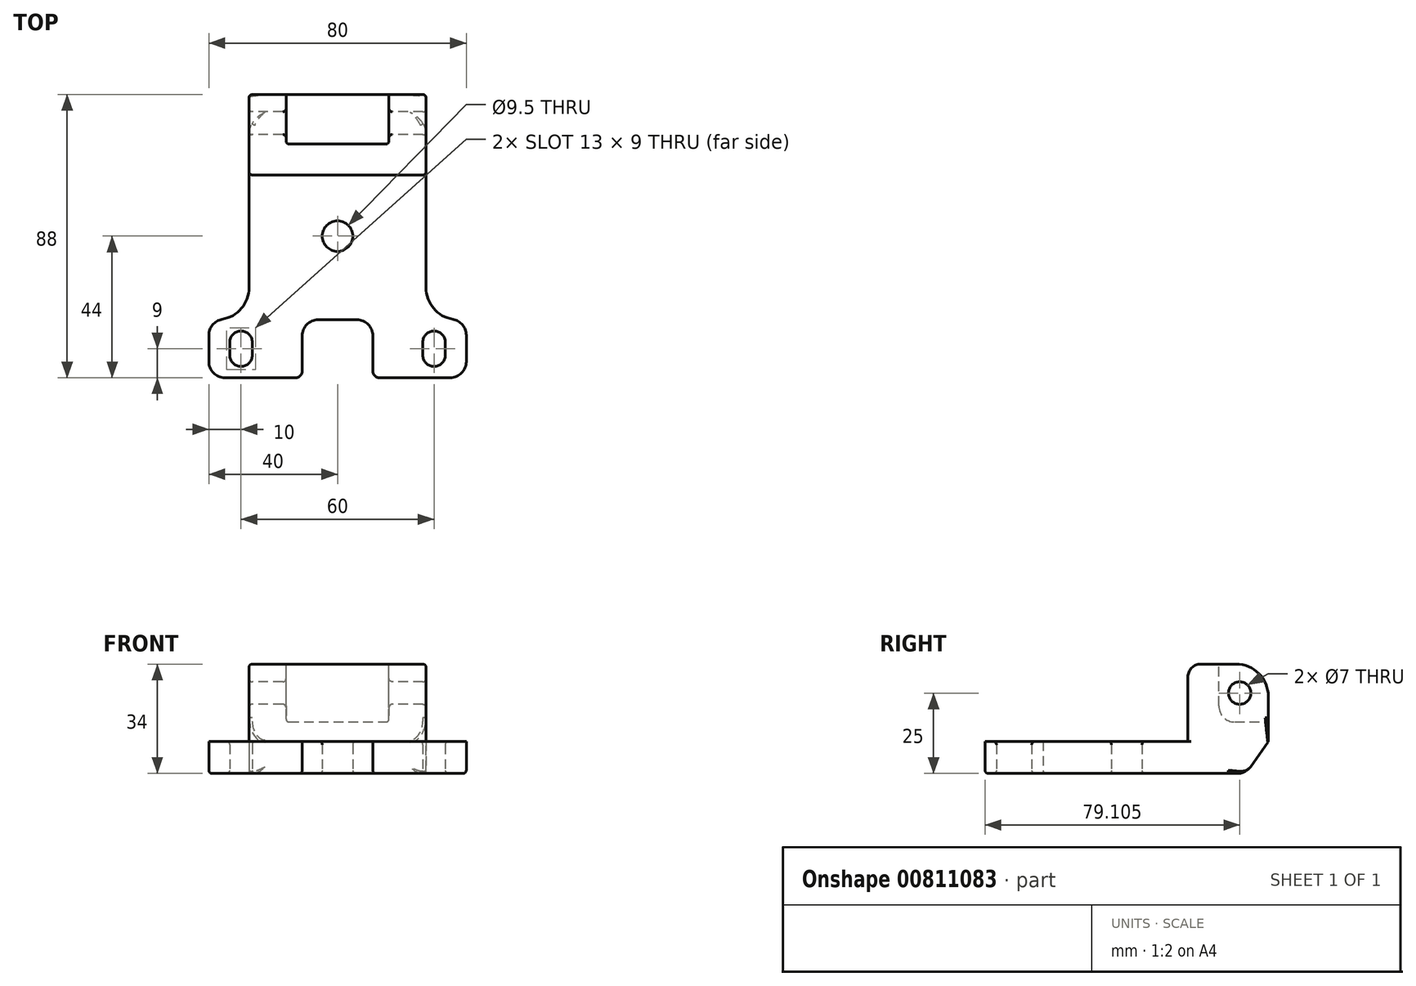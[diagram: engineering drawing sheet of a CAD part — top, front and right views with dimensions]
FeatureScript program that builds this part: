
annotation { "Feature Type Name" : "Feature", "Feature Type Description" : "" }
export const myFeature = defineFeature(function(context is Context, id is Id, definition is map)
    precondition{}
    {
        {
            var Q0;
            Q0=qCreatedBy(makeId("Top.planeOp"),FACE);
            var sketch = newSketch(context, id + "F0", { "sketchPlane" : qUnion([Q0])});
            skLineSegment(sketch, "E0.bottom", {"start": v(-40, 9) * mm, "end": v(-37.5, 9) * mm});
            skLineSegment(sketch, "E0.top", {"start": v(-40, -9) * mm, "end": v(40, -9) * mm});
            skLineSegment(sketch, "E0.left", {"start": v(-40, 9) * mm, "end": v(-40, -9) * mm});
            skLineSegment(sketch, "E0.right", {"start": v(40, 9) * mm, "end": v(40, -9) * mm});
            skPoint(sketch, "E0.middle", {"position": v(0, 0) * mm});
            skLineSegment(sketch, "E1.bottom", {"start": v(37.5, 9) * mm, "end": v(40, 9) * mm});
            skLineSegment(sketch, "E1.top", {"start": v(-27.5, 79) * mm, "end": v(27.5, 79) * mm});
            skLineSegment(sketch, "E1.left", {"start": v(-27.5, 19) * mm, "end": v(-27.5, 79) * mm});
            skLineSegment(sketch, "E1.right", {"start": v(27.5, 19) * mm, "end": v(27.5, 79) * mm});
            skLineSegment(sketch, "E2", {"start": v(0, 0) * mm, "end": v(0, 68.92) * mm, "construction": true});
            skCircle(sketch, "E3", {"center": v(0, 35) * mm, "radius": 4.75 * mm});
            skPoint(sketch, "E4.newPointA", {"position": v(40, 9) * mm});
            skArc(sketch, "E4.filletArc", {"start": v(-37.5, 9) * mm, "mid": v(-30.43, 11.93) * mm, "end": v(-27.5, 19) * mm});
            skPoint(sketch, "E5.visualSharp", {"position": v(27.5, 9) * mm});
            skArc(sketch, "E5.filletArc", {"start": v(27.5, 19) * mm, "mid": v(30.43, 11.93) * mm, "end": v(37.5, 9) * mm});
            skLineSegment(sketch, "E6.bottom", {"start": v(11, 9) * mm, "end": v(-11, 9) * mm});
            skLineSegment(sketch, "E6.top", {"start": v(11, -27) * mm, "end": v(-11, -27) * mm});
            skLineSegment(sketch, "E6.left", {"start": v(11, 9) * mm, "end": v(11, -27) * mm});
            skLineSegment(sketch, "E6.right", {"start": v(-11, 9) * mm, "end": v(-11, -27) * mm});
            skPoint(sketch, "E6.middle", {"position": v(0, -9) * mm});
            skLineSegment(sketch, "E7", {"start": v(-40, 0) * mm, "end": v(40, 0) * mm, "construction": true});
            skCircle(sketch, "E8", {"center": v(-30, 0) * mm, "radius": 3.5 * mm, "construction": true});
            skCircle(sketch, "E9", {"center": v(30, 0) * mm, "radius": 3.5 * mm, "construction": true});
            skLineSegment(sketch, "E10.bottom", {"start": v(-26.5, 2) * mm, "end": v(-33.5, 2) * mm});
            skLineSegment(sketch, "E10.top", {"start": v(-26.5, -2) * mm, "end": v(-33.5, -2) * mm});
            skLineSegment(sketch, "E10.left", {"start": v(-26.5, 2) * mm, "end": v(-26.5, -2) * mm});
            skLineSegment(sketch, "E10.right", {"start": v(-33.5, 2) * mm, "end": v(-33.5, -2) * mm});
            skLineSegment(sketch, "E11.bottom", {"start": v(26.5, 2) * mm, "end": v(33.5, 2) * mm});
            skLineSegment(sketch, "E11.top", {"start": v(26.5, -2) * mm, "end": v(33.5, -2) * mm});
            skLineSegment(sketch, "E11.left", {"start": v(26.5, 2) * mm, "end": v(26.5, -2) * mm});
            skLineSegment(sketch, "E11.right", {"start": v(33.5, 2) * mm, "end": v(33.5, -2) * mm});
            skArc(sketch, "E12", {"start": v(-26.5, 2) * mm, "mid": v(-30, 5.5) * mm, "end": v(-33.5, 2) * mm});
            skArc(sketch, "E13", {"start": v(-33.5, -2) * mm, "mid": v(-30, -5.5) * mm, "end": v(-26.5, -2) * mm});
            skArc(sketch, "E14", {"start": v(33.5, 2) * mm, "mid": v(30, 5.5) * mm, "end": v(26.5, 2) * mm});
            skArc(sketch, "E15", {"start": v(26.5, -2) * mm, "mid": v(30, -5.5) * mm, "end": v(33.5, -2) * mm});
            skSolve(sketch);
        }
        {
            var Q0;
            Q0=makeQuery(id+"F0.imprint","IMPRINT",FACE,{"disambiguationData":[TD([[makeQuery(id+"F0.imprint","IMPRINT",EDGE,{"derivedFrom":sQuery(id+"F0.wireOp",EDGE,"E0.bottom")}),-1.0]])]});
            extrude(context, id + "F1", {"entities" : qUnion([Q0]), "depth" : 10 * mm, "offsetDistance" : 25 * mm});
        }
        {
            var Q0;
            Q0=makeQuery(id+"F1.opExtrude","SWEPT_EDGE",EDGE,{"disambiguationData":[OSD([sQuery(id+"F0.wireOp",EDGE,"E6.bottom"),sQuery(id+"F0.wireOp",EDGE,"E6.left")])]});
            var Q1;
            Q1=makeQuery(id+"F1.opExtrude","SWEPT_EDGE",EDGE,{"disambiguationData":[OSD([sQuery(id+"F0.wireOp",EDGE,"E6.bottom"),sQuery(id+"F0.wireOp",EDGE,"E6.right")])]});
            var Q2;
            Q2=makeQuery(id+"F1.opExtrude","SWEPT_EDGE",EDGE,{"disambiguationData":[OSD([sQuery(id+"F0.wireOp",EDGE,"E0.top"),sQuery(id+"F0.wireOp",EDGE,"E0.right")])]});
            var Q3;
            Q3=makeQuery(id+"F1.opExtrude","SWEPT_EDGE",EDGE,{"disambiguationData":[OSD([sQuery(id+"F0.wireOp",EDGE,"E0.right"),sQuery(id+"F0.wireOp",EDGE,"E1.bottom")])]});
            var Q4;
            Q4=makeQuery(id+"F1.opExtrude","SWEPT_EDGE",EDGE,{"disambiguationData":[OSD([sQuery(id+"F0.wireOp",EDGE,"E0.top"),sQuery(id+"F0.wireOp",EDGE,"E0.left")])]});
            var Q5;
            Q5=makeQuery(id+"F1.opExtrude","SWEPT_EDGE",EDGE,{"disambiguationData":[OSD([sQuery(id+"F0.wireOp",EDGE,"E0.bottom"),sQuery(id+"F0.wireOp",EDGE,"E0.left")])]});
            fillet(context, id + "F2", {"entities" : qUnion([Q0, Q1, Q2, Q3, Q4, Q5]), "radius" : 5 * mm, "tangentPropagation" : true, "allowEdgeOverflow" : false});
        }
        {
            var Q0;
            Q0=makeQuery(id+"F1.opExtrude","SWEPT_EDGE",EDGE,{"disambiguationData":[OSD([sQuery(id+"F0.wireOp",EDGE,"E0.top"),sQuery(id+"F0.wireOp",EDGE,"E6.left")])]});
            var Q1;
            Q1=makeQuery(id+"F1.opExtrude","SWEPT_EDGE",EDGE,{"disambiguationData":[OSD([sQuery(id+"F0.wireOp",EDGE,"E0.top"),sQuery(id+"F0.wireOp",EDGE,"E6.right")])]});
            fillet(context, id + "F3", {"entities" : qUnion([Q0, Q1]), "radius" : 2 * mm, "tangentPropagation" : true, "allowEdgeOverflow" : false});
        }
        {
            var Q0;
            Q0=makeQuery(id+"F1.opExtrude","CAP_FACE",FACE,{"disambiguationData":[OSD([sQuery(id+"F0.wireOp",EDGE,"E0.bottom"),sQuery(id+"F0.wireOp",EDGE,"E0.top"),sQuery(id+"F0.wireOp",EDGE,"E0.left"),sQuery(id+"F0.wireOp",EDGE,"E0.right"),sQuery(id+"F0.wireOp",EDGE,"E1.bottom"),sQuery(id+"F0.wireOp",EDGE,"E1.top"),sQuery(id+"F0.wireOp",EDGE,"E1.left"),sQuery(id+"F0.wireOp",EDGE,"E1.right"),sQuery(id+"F0.wireOp",EDGE,"E3"),sQuery(id+"F0.wireOp",EDGE,"E4.filletArc"),sQuery(id+"F0.wireOp",EDGE,"E5.filletArc"),sQuery(id+"F0.wireOp",EDGE,"E6.bottom"),sQuery(id+"F0.wireOp",EDGE,"E6.left"),sQuery(id+"F0.wireOp",EDGE,"E6.right"),sQuery(id+"F0.wireOp",EDGE,"E8"),sQuery(id+"F0.wireOp",EDGE,"E9")])],"isStart":false});
            var sketch = newSketch(context, id + "F4", { "sketchPlane" : qUnion([Q0])});
            skLineSegment(sketch, "E16.bottom", {"start": v(27.5, 79) * mm, "end": v(-27.5, 79) * mm});
            skLineSegment(sketch, "E16.top", {"start": v(27.5, 54) * mm, "end": v(-27.5, 54) * mm});
            skLineSegment(sketch, "E16.left", {"start": v(27.5, 79) * mm, "end": v(27.5, 54) * mm});
            skLineSegment(sketch, "E16.right", {"start": v(-27.5, 79) * mm, "end": v(-27.5, 54) * mm});
            skSolve(sketch);
        }
        {
            var Q0;
            Q0 = qSketchRegion(id + "F4", true);
            extrude(context, id + "F5", {"entities" : qUnion([Q0]), "operationType" : NewBodyOperationType.ADD, "depth" : 24 * mm, "offsetDistance" : 25 * mm});
        }
        {
            var Q0;
            Q0=makeQuery(id+"F5.boolean.opBoolean","MERGE",FACE,{"derivedFrom":[makeQuery(id+"F1.opExtrude","SWEPT_FACE",FACE,{"disambiguationData":[OSD([sQuery(id+"F0.wireOp",EDGE,"E1.left")])]}),makeQuery(id+"F5.opExtrude","SWEPT_FACE",FACE,{"disambiguationData":[OSD([sQuery(id+"F4.wireOp",EDGE,"E16.right")])]})]});
            var sketch = newSketch(context, id + "F6", { "sketchPlane" : qUnion([Q0])});
            skCircle(sketch, "E17", {"center": v(-70.1, 25) * mm, "radius": 3.5 * mm});
            skLineSegment(sketch, "E18", {"start": v(-66.5, 34) * mm, "end": v(-70.1, 25) * mm, "construction": true});
            skSolve(sketch);
        }
        {
            var Q0;
            Q0 = qSketchRegion(id + "F6", true);
            extrude(context, id + "F7", {"entities" : qUnion([Q0]), "operationType" : NewBodyOperationType.REMOVE, "endBound" : BoundingType.THROUGH_ALL, "oppositeDirection" : true, "depth" : 25 * mm, "offsetDistance" : 25 * mm});
        }
        {
            var Q0;
            {var subQ0=sQuery(id+"F4.wireOp",EDGE,"E16.bottom");var subQ1=sQuery(id+"F4.wireOp",EDGE,"E16.left");var subQ2=sQuery(id+"F4.wireOp",EDGE,"E16.right");Q0=makeQuery(id+"F7.boolean.opBoolean","SPLIT",FACE,{"disambiguationData":[TD([makeQuery(id+"F1.opExtrude","SWEPT_FACE",FACE,{"disambiguationData":[OSD([sQuery(id+"F0.wireOp",EDGE,"E1.top")])]})])],"derivedFrom":makeQuery(id+"F5.opExtrude","CAP_FACE",FACE,{"disambiguationData":[OSD([subQ0,sQuery(id+"F4.wireOp",EDGE,"E16.top"),subQ1,subQ2])],"isStart":false})});}
            var sketch = newSketch(context, id + "F8", { "sketchPlane" : qUnion([Q0])});
            skLineSegment(sketch, "E19.bottom", {"start": v(-16, 63.6) * mm, "end": v(16, 63.6) * mm});
            skLineSegment(sketch, "E19.top", {"start": v(-16, 94.4) * mm, "end": v(16, 94.4) * mm});
            skLineSegment(sketch, "E19.left", {"start": v(-16, 63.6) * mm, "end": v(-16, 94.4) * mm});
            skLineSegment(sketch, "E19.right", {"start": v(16, 63.6) * mm, "end": v(16, 94.4) * mm});
            skPoint(sketch, "E19.middle", {"position": v(0, 79) * mm});
            skSolve(sketch);
        }
        {
            var Q0;
            {var subQ0=sQuery(id+"F8.wireOp",EDGE,"E19.left");var subQ1=sQuery(id+"F4.wireOp",EDGE,"E16.bottom");var subQ4=makeQuery(id+"F5.opExtrude","CAP_EDGE",EDGE,{"disambiguationData":[OSD([subQ1])],"isStart":false});var subQ5=makeQuery(id+"F8.imprint","INTERSECT",VERTEX,{"derivedFrom":[subQ4,subQ0]});Q0=makeQuery(id+"F8.imprint","IMPRINT",FACE,{"disambiguationData":[TD([[makeQuery(id+"F8.imprint","IMPRINT",EDGE,{"disambiguationData":[TD([[subQ5,-1.0]])],"derivedFrom":subQ4}),-1.0]])]});}
            var Q1;
            {var subQ0=sQuery(id+"F8.wireOp",EDGE,"E19.bottom");Q1=makeQuery(id+"F8.imprint","IMPRINT",FACE,{"disambiguationData":[TD([[makeQuery(id+"F8.imprint","IMPRINT",EDGE,{"derivedFrom":subQ0}),1.0]])]});}
            extrude(context, id + "F9", {"entities" : qUnion([Q0, Q1]), "operationType" : NewBodyOperationType.REMOVE, "oppositeDirection" : true, "depth" : 18 * mm, "offsetDistance" : 25 * mm});
        }
        {
            var Q0;
            Q0=makeQuery(id+"F9.boolean.opBoolean","COPY",EDGE,{"derivedFrom":makeQuery(id+"F9.opExtrude","CAP_EDGE",EDGE,{"disambiguationData":[OSD([sQuery(id+"F8.wireOp",EDGE,"E19.bottom")])],"isStart":false})});
            var Q1;
            Q1=makeQuery(id+"F9.boolean.opBoolean","COPY",EDGE,{"derivedFrom":makeQuery(id+"F9.opExtrude","CAP_EDGE",EDGE,{"disambiguationData":[OSD([sQuery(id+"F4.wireOp",EDGE,"E16.bottom")])],"isStart":false})});
            fillet(context, id + "F10", {"entities" : qUnion([Q0, Q1]), "radius" : 5 * mm, "tangentPropagation" : true, "allowEdgeOverflow" : false});
        }
        {
            var Q0;
            Q0=makeQuery(id+"F5.opExtrude","CAP_EDGE",EDGE,{"disambiguationData":[OSD([sQuery(id+"F4.wireOp",EDGE,"E16.top")])],"isStart":true});
            var Q1;
            {var subQ1=sQuery(id+"F4.wireOp",EDGE,"E16.bottom");Q1=makeQuery(id+"F9.boolean.opBoolean","SPLIT",EDGE,{"disambiguationData":[TD([makeQuery(id+"F1.opExtrude","SWEPT_FACE",FACE,{"disambiguationData":[OSD([sQuery(id+"F0.wireOp",EDGE,"E1.left")])]})])],"derivedFrom":makeQuery(id+"F5.opExtrude","CAP_EDGE",EDGE,{"disambiguationData":[OSD([subQ1])],"isStart":false})});}
            var Q2;
            {var subQ1=sQuery(id+"F4.wireOp",EDGE,"E16.bottom");Q2=makeQuery(id+"F9.boolean.opBoolean","SPLIT",EDGE,{"disambiguationData":[TD([makeQuery(id+"F1.opExtrude","SWEPT_FACE",FACE,{"disambiguationData":[OSD([sQuery(id+"F0.wireOp",EDGE,"E1.right")])]})])],"derivedFrom":makeQuery(id+"F5.opExtrude","CAP_EDGE",EDGE,{"disambiguationData":[OSD([subQ1])],"isStart":false})});}
            fillet(context, id + "F11", {"entities" : qUnion([Q0, Q1, Q2]), "radius" : 10 * mm, "tangentPropagation" : true, "allowEdgeOverflow" : false});
        }
        {
            var Q0;
            Q0=makeQuery(id+"F5.opExtrude","CAP_EDGE",EDGE,{"disambiguationData":[OSD([sQuery(id+"F4.wireOp",EDGE,"E16.top")])],"isStart":false});
            var Q1;
            Q1=makeQuery(id+"F9.boolean.opBoolean","COPY",EDGE,{"derivedFrom":makeQuery(id+"F9.opExtrude","CAP_EDGE",EDGE,{"disambiguationData":[OSD([sQuery(id+"F8.wireOp",EDGE,"E19.bottom")])],"isStart":true})});
            fillet(context, id + "F12", {"entities" : qUnion([Q0, Q1]), "radius" : 4 * mm, "tangentPropagation" : true, "allowEdgeOverflow" : false});
        }
        {
            var Q0;
            Q0=makeQuery(id+"F1.opExtrude","CAP_EDGE",EDGE,{"disambiguationData":[OSD([sQuery(id+"F0.wireOp",EDGE,"E1.top")])],"isStart":true});
            chamfer(context, id + "F13", {"entities" : qUnion([Q0]), "chamferType" : ChamferType.TWO_OFFSETS, "width1" : 7 * mm, "oppositeDirection" : false, "width2" : 10 * mm, "tangentPropagation" : true});
        }
        {
            var Q0;
            Q0=makeQuery(id+"F9.boolean.opBoolean","SPLIT",FACE,{"disambiguationData":[TD([makeQuery(id+"F1.opExtrude","SWEPT_FACE",FACE,{"disambiguationData":[OSD([sQuery(id+"F0.wireOp",EDGE,"E1.right")])]})])],"derivedFrom":makeQuery(id+"F7.boolean.opBoolean","COPY",FACE,{"derivedFrom":makeQuery(id+"F7.opExtrude","SWEPT_FACE",FACE,{"disambiguationData":[OSD([sQuery(id+"F6.wireOp",EDGE,"E17")])]})})});
            var Q1;
            Q1=makeQuery(id+"F9.boolean.opBoolean","SPLIT",FACE,{"disambiguationData":[TD([makeQuery(id+"F1.opExtrude","SWEPT_FACE",FACE,{"disambiguationData":[OSD([sQuery(id+"F0.wireOp",EDGE,"E1.left")])]})])],"derivedFrom":makeQuery(id+"F7.boolean.opBoolean","COPY",FACE,{"derivedFrom":makeQuery(id+"F7.opExtrude","SWEPT_FACE",FACE,{"disambiguationData":[OSD([sQuery(id+"F6.wireOp",EDGE,"E17")])]})})});
            var Q2;
            Q2=makeQuery(id+"F1.opExtrude","SWEPT_FACE",FACE,{"disambiguationData":[OSD([sQuery(id+"F0.wireOp",EDGE,"E9")])]});
            var Q3;
            Q3=makeQuery(id+"F1.opExtrude","SWEPT_FACE",FACE,{"disambiguationData":[OSD([sQuery(id+"F0.wireOp",EDGE,"E8")])]});
            var Q4;
            Q4=makeQuery(id+"F1.opExtrude","SWEPT_FACE",FACE,{"disambiguationData":[OSD([sQuery(id+"F0.wireOp",EDGE,"E3")])]});
            var Q5;
            {var subQ0=sQuery(id+"F4.wireOp",EDGE,"E16.right");var subQ1=makeQuery(id+"F5.opExtrude","SWEPT_FACE",FACE,{"disambiguationData":[OSD([subQ0])]});var subQ2=makeQuery(id+"F1.opExtrude","SWEPT_FACE",FACE,{"disambiguationData":[OSD([sQuery(id+"F0.wireOp",EDGE,"E1.left")])]});var subQ3=sQuery(id+"F4.wireOp",EDGE,"E16.bottom");Q5=makeQuery(id+"F11.opFillet","BLEND_EDGE",EDGE,{"blendedFrom":[makeQuery(id+"F9.boolean.opBoolean","SPLIT",EDGE,{"disambiguationData":[TD([subQ2])],"derivedFrom":makeQuery(id+"F5.opExtrude","CAP_EDGE",EDGE,{"disambiguationData":[OSD([subQ3])],"isStart":false})}),makeQuery(id+"F5.boolean.opBoolean","MERGE",FACE,{"derivedFrom":[subQ2,subQ1]})],"blendedInto":[makeQuery(id+"F5.boolean.opBoolean","MERGE",FACE,{"derivedFrom":[subQ2,subQ1]})]});}
            var Q6;
            {var subQ0=sQuery(id+"F4.wireOp",EDGE,"E16.left");var subQ1=makeQuery(id+"F5.opExtrude","SWEPT_FACE",FACE,{"disambiguationData":[OSD([subQ0])]});var subQ2=makeQuery(id+"F1.opExtrude","SWEPT_FACE",FACE,{"disambiguationData":[OSD([sQuery(id+"F0.wireOp",EDGE,"E1.right")])]});var subQ3=sQuery(id+"F4.wireOp",EDGE,"E16.bottom");Q6=makeQuery(id+"F11.opFillet","BLEND_EDGE",EDGE,{"blendedFrom":[makeQuery(id+"F9.boolean.opBoolean","SPLIT",EDGE,{"disambiguationData":[TD([subQ2])],"derivedFrom":makeQuery(id+"F5.opExtrude","CAP_EDGE",EDGE,{"disambiguationData":[OSD([subQ3])],"isStart":false})}),makeQuery(id+"F5.boolean.opBoolean","MERGE",FACE,{"derivedFrom":[subQ2,subQ1]})],"blendedInto":[makeQuery(id+"F5.boolean.opBoolean","MERGE",FACE,{"derivedFrom":[subQ2,subQ1]})]});}
            var Q7;
            Q7=makeQuery(id+"F9.boolean.opBoolean","COPY",EDGE,{"derivedFrom":makeQuery(id+"F9.opExtrude","SWEPT_EDGE",EDGE,{"disambiguationData":[OSD([sQuery(id+"F4.wireOp",EDGE,"E16.bottom"),sQuery(id+"F8.wireOp",EDGE,"E19.right")])]})});
            var Q8;
            Q8=makeQuery(id+"F9.boolean.opBoolean","COPY",EDGE,{"derivedFrom":makeQuery(id+"F9.opExtrude","SWEPT_EDGE",EDGE,{"disambiguationData":[OSD([sQuery(id+"F4.wireOp",EDGE,"E16.bottom"),sQuery(id+"F8.wireOp",EDGE,"E19.left")])]})});
            var Q9;
            {var subQ0=sQuery(id+"F0.wireOp",EDGE,"E1.top");Q9=makeQuery(id+"F13.opChamfer","BLEND_EDGE",EDGE,{"blendedFrom":[makeQuery(id+"F1.opExtrude","CAP_EDGE",EDGE,{"disambiguationData":[OSD([subQ0])],"isStart":true}),makeQuery(id+"F5.boolean.opBoolean","MERGE",FACE,{"derivedFrom":[makeQuery(id+"F1.opExtrude","SWEPT_FACE",FACE,{"disambiguationData":[OSD([subQ0])]}),makeQuery(id+"F5.opExtrude","SWEPT_FACE",FACE,{"disambiguationData":[OSD([sQuery(id+"F4.wireOp",EDGE,"E16.bottom")])]})]})],"blendedInto":[makeQuery(id+"F5.boolean.opBoolean","MERGE",FACE,{"derivedFrom":[makeQuery(id+"F1.opExtrude","SWEPT_FACE",FACE,{"disambiguationData":[OSD([subQ0])]}),makeQuery(id+"F5.opExtrude","SWEPT_FACE",FACE,{"disambiguationData":[OSD([sQuery(id+"F4.wireOp",EDGE,"E16.bottom")])]})]})]});}
            var Q10;
            Q10=makeQuery(id+"F1.opExtrude","CAP_EDGE",EDGE,{"disambiguationData":[OSD([sQuery(id+"F0.wireOp",EDGE,"E4.filletArc")])],"isStart":true});
            var Q11;
            Q11=makeQuery(id+"F1.opExtrude","SWEPT_FACE",FACE,{"disambiguationData":[OSD([sQuery(id+"F0.wireOp",EDGE,"E14")])]});
            var Q12;
            Q12=makeQuery(id+"F1.opExtrude","SWEPT_FACE",FACE,{"disambiguationData":[OSD([sQuery(id+"F0.wireOp",EDGE,"E12")])]});
            fillet(context, id + "F14", {"entities" : qUnion([Q0, Q1, Q2, Q3, Q4, Q5, Q6, Q7, Q8, Q9, Q10, Q11, Q12]), "radius" : 1 * mm, "tangentPropagation" : true, "allowEdgeOverflow" : false});
        }
        {
            var Q0;
            Q0=makeQuery(id+"F10.opFillet","BLEND_EDGE",EDGE,{"blendedFrom":[makeQuery(id+"F9.boolean.opBoolean","COPY",EDGE,{"derivedFrom":makeQuery(id+"F9.opExtrude","CAP_EDGE",EDGE,{"disambiguationData":[OSD([sQuery(id+"F8.wireOp",EDGE,"E19.bottom")])],"isStart":false})}),makeQuery(id+"F9.boolean.opBoolean","COPY",FACE,{"derivedFrom":makeQuery(id+"F9.opExtrude","SWEPT_FACE",FACE,{"disambiguationData":[OSD([sQuery(id+"F8.wireOp",EDGE,"E19.left")])]})})],"blendedInto":[makeQuery(id+"F9.boolean.opBoolean","COPY",FACE,{"derivedFrom":makeQuery(id+"F9.opExtrude","SWEPT_FACE",FACE,{"disambiguationData":[OSD([sQuery(id+"F8.wireOp",EDGE,"E19.left")])]})})]});
            var Q1;
            Q1=makeQuery(id+"F10.opFillet","BLEND_EDGE",EDGE,{"blendedFrom":[makeQuery(id+"F9.boolean.opBoolean","COPY",EDGE,{"derivedFrom":makeQuery(id+"F9.opExtrude","CAP_EDGE",EDGE,{"disambiguationData":[OSD([sQuery(id+"F8.wireOp",EDGE,"E19.bottom")])],"isStart":false})}),makeQuery(id+"F9.boolean.opBoolean","COPY",FACE,{"derivedFrom":makeQuery(id+"F9.opExtrude","SWEPT_FACE",FACE,{"disambiguationData":[OSD([sQuery(id+"F8.wireOp",EDGE,"E19.right")])]})})],"blendedInto":[makeQuery(id+"F9.boolean.opBoolean","COPY",FACE,{"derivedFrom":makeQuery(id+"F9.opExtrude","SWEPT_FACE",FACE,{"disambiguationData":[OSD([sQuery(id+"F8.wireOp",EDGE,"E19.right")])]})})]});
            fillet(context, id + "F15", {"entities" : qUnion([Q0, Q1]), "radius" : 1 * mm, "tangentPropagation" : true, "allowEdgeOverflow" : false});
        }
        {
            var Q0;
            Q0=makeQuery(id+"F13.opChamfer","BLEND_EDGE",EDGE,{"blendedFrom":[makeQuery(id+"F1.opExtrude","CAP_EDGE",EDGE,{"disambiguationData":[OSD([sQuery(id+"F0.wireOp",EDGE,"E1.top")])],"isStart":true}),makeQuery(id+"F5.boolean.opBoolean","MERGE",FACE,{"derivedFrom":[makeQuery(id+"F1.opExtrude","SWEPT_FACE",FACE,{"disambiguationData":[OSD([sQuery(id+"F0.wireOp",EDGE,"E1.right")])]}),makeQuery(id+"F5.opExtrude","SWEPT_FACE",FACE,{"disambiguationData":[OSD([sQuery(id+"F4.wireOp",EDGE,"E16.left")])]})]})],"blendedInto":[makeQuery(id+"F5.boolean.opBoolean","MERGE",FACE,{"derivedFrom":[makeQuery(id+"F1.opExtrude","SWEPT_FACE",FACE,{"disambiguationData":[OSD([sQuery(id+"F0.wireOp",EDGE,"E1.right")])]}),makeQuery(id+"F5.opExtrude","SWEPT_FACE",FACE,{"disambiguationData":[OSD([sQuery(id+"F4.wireOp",EDGE,"E16.left")])]})]})]});
            fillet(context, id + "F16", {"entities" : qUnion([Q0]), "radius" : 5 * mm, "tangentPropagation" : true, "allowEdgeOverflow" : false});
        }
    });
